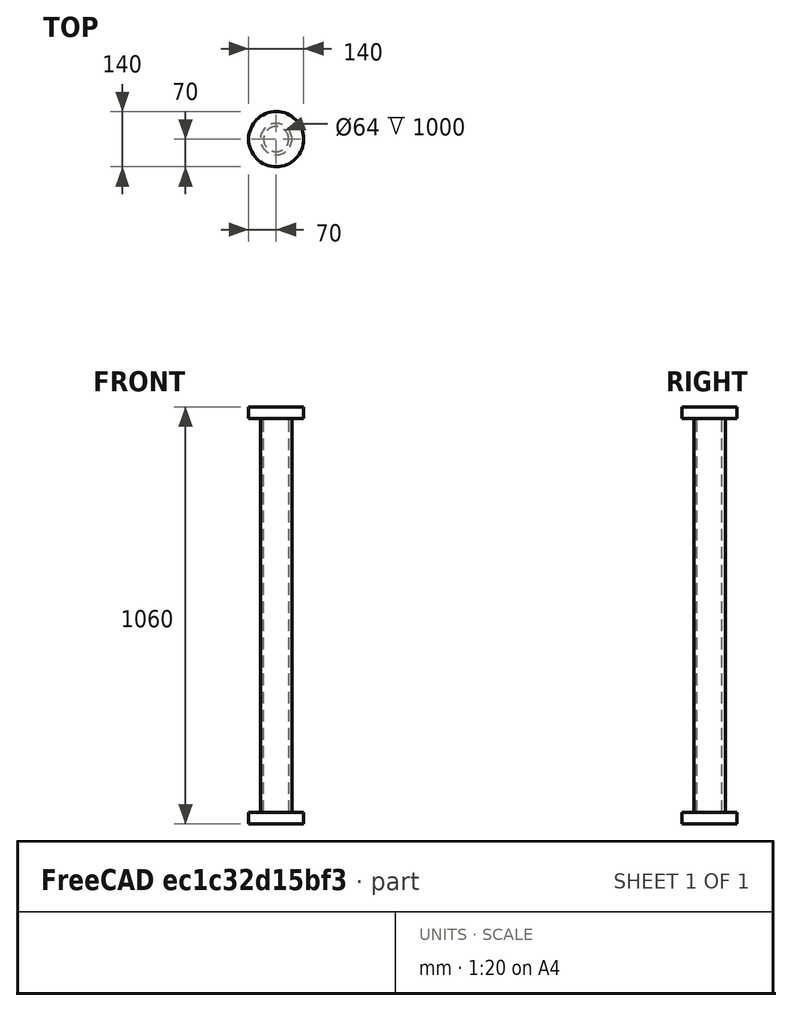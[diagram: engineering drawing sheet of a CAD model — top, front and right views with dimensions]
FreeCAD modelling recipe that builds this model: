
FCSTD DOCUMENT  (FreeCAD 0.19R)
Label: model
License: All rights reserved
LicenseURL: http://en.wikipedia.org/wiki/All_rights_reserved
objects: Mesh::Feature×3, Part::Cylinder×2, Part::FeaturePython×1
note: 3 computed .brp shape members not serialized (recipe doc carries the construction recipe); baked Part::Feature solids carry a one-line shape summary decoded from their .brp

FEATURE [Part::FeaturePython] Tube  # WARN: FeaturePython — macro-defined, semantics opaque (R4)
  AttacherType = Attacher::AttachEngine3D
  Height = 1000
  InnerRadius = 32
  OuterRadius = 40
FEATURE [Part::Cylinder] Cylinder001
  Angle = 360
  AttacherType = Attacher::AttachEngine3D
  Height = 30
  Placement = pos=(0,0,-30) rot=(0,0,1;0rad)
  Radius = 70
FEATURE [Part::Cylinder] Cylinder003
  Angle = 360
  AttacherType = Attacher::AttachEngine3D
  Height = 30
  Placement = pos=(0,0,1000) rot=(0,0,1;0rad)
  Radius = 70
FEATURE [Mesh::Feature] Mesh  label="Tube (Meshed)"
FEATURE [Mesh::Feature] Mesh001  label="Cylinder001 (Meshed)"
FEATURE [Mesh::Feature] Mesh002  label="Cylinder003 (Meshed)"
